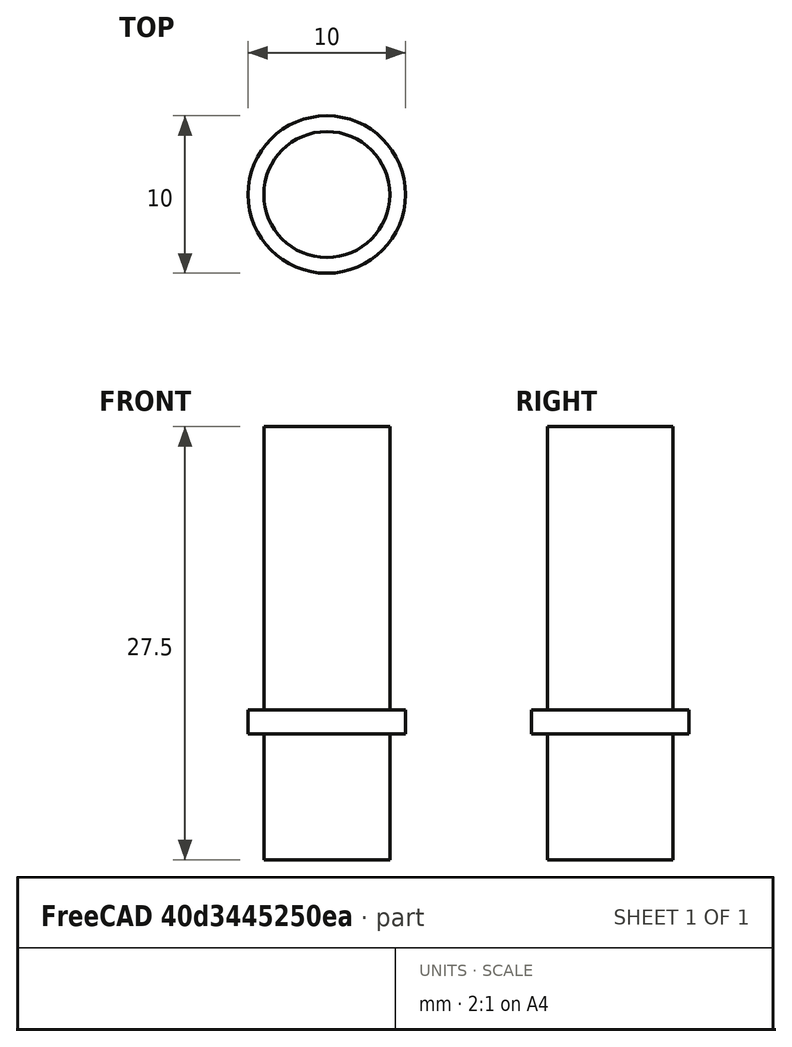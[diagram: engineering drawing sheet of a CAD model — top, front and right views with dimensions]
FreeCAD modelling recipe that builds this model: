
FCSTD DOCUMENT  (FreeCAD 0.20R29177 +426 (Git))
Label: FilamentSpoolExtendedBallBearingPin
License: All rights reserved
LicenseURL: http://en.wikipedia.org/wiki/All_rights_reserved
objects: Sketcher::SketchObject×1, PartDesign::Revolution×1, PartDesign::Body×1
note: 4 computed .brp shape members not serialized (recipe doc carries the construction recipe); baked Part::Feature solids carry a one-line shape summary decoded from their .brp

FEATURE [Sketcher::SketchObject] Sketch
  FullyConstrained = true
  MapMode = 5
  Placement = pos=(0,0,0) rot=(1,0,0;1.5708rad)
  Support = -> [XZ_Plane]
  sketch-geometry (8):
    g0: LineSegment StartX=0 StartY=0 StartZ=0 EndX=4 EndY=0 EndZ=0
    g1: LineSegment StartX=4 StartY=0 StartZ=0 EndX=4 EndY=8 EndZ=0
    g2: LineSegment StartX=4 StartY=8 StartZ=0 EndX=5 EndY=8 EndZ=0
    g3: LineSegment StartX=5 StartY=8 StartZ=0 EndX=5 EndY=9.5 EndZ=0
    g4: LineSegment StartX=5 StartY=9.5 StartZ=0 EndX=4 EndY=9.5 EndZ=0
    g5: LineSegment StartX=4 StartY=9.5 StartZ=0 EndX=4 EndY=27.5 EndZ=0
    g6: LineSegment StartX=4 StartY=27.5 StartZ=0 EndX=0 EndY=27.5 EndZ=0
    g7: LineSegment StartX=0 StartY=27.5 StartZ=0 EndX=0 EndY=0 EndZ=0
  constraints (23):
    c: Coincident(g-1,g0)
    c: Horizontal(g0)
    c: Coincident(g0,g1)
    c: Vertical(g1)
    c: Coincident(g1,g2)
    c: Horizontal(g2)
    c: Coincident(g2,g3)
    c: Vertical(g3)
    c: Coincident(g3,g4)
    c: Coincident(g4,g5)
    c: Vertical(g5)
    c: Coincident(g5,g6)
    c: PointOnObject(g6,g-2)
    c: Horizontal(g6)
    c: Coincident(g6,g7)
    c: Coincident(g7,g0)
    c: DistanceX(g0,g0) = 4
    c: Vertical(g1,g5)
    c: Horizontal(g4)
    c: DistanceX(g0,g2) = 5
    c: DistanceY(g1,g1) = 8
    c: DistanceY(g3,g3) = 1.5
    c: DistanceY(g5,g5) = 18
FEATURE [PartDesign::Revolution] Revolution
  Angle = 360
  Axis = (0,2e-16,1)
  Base = (0,0,0)
  Placement = pos=(0,0,0) rot=(1,0,0;1.5708rad)
  Profile = -> Sketch
  ReferenceAxis = -> Sketch [V_Axis]
  Reversed = true
FEATURE [PartDesign::Body] Body
  Group = -> [Sketch,Revolution]
  Origin = -> Origin
  Tip = -> Revolution
